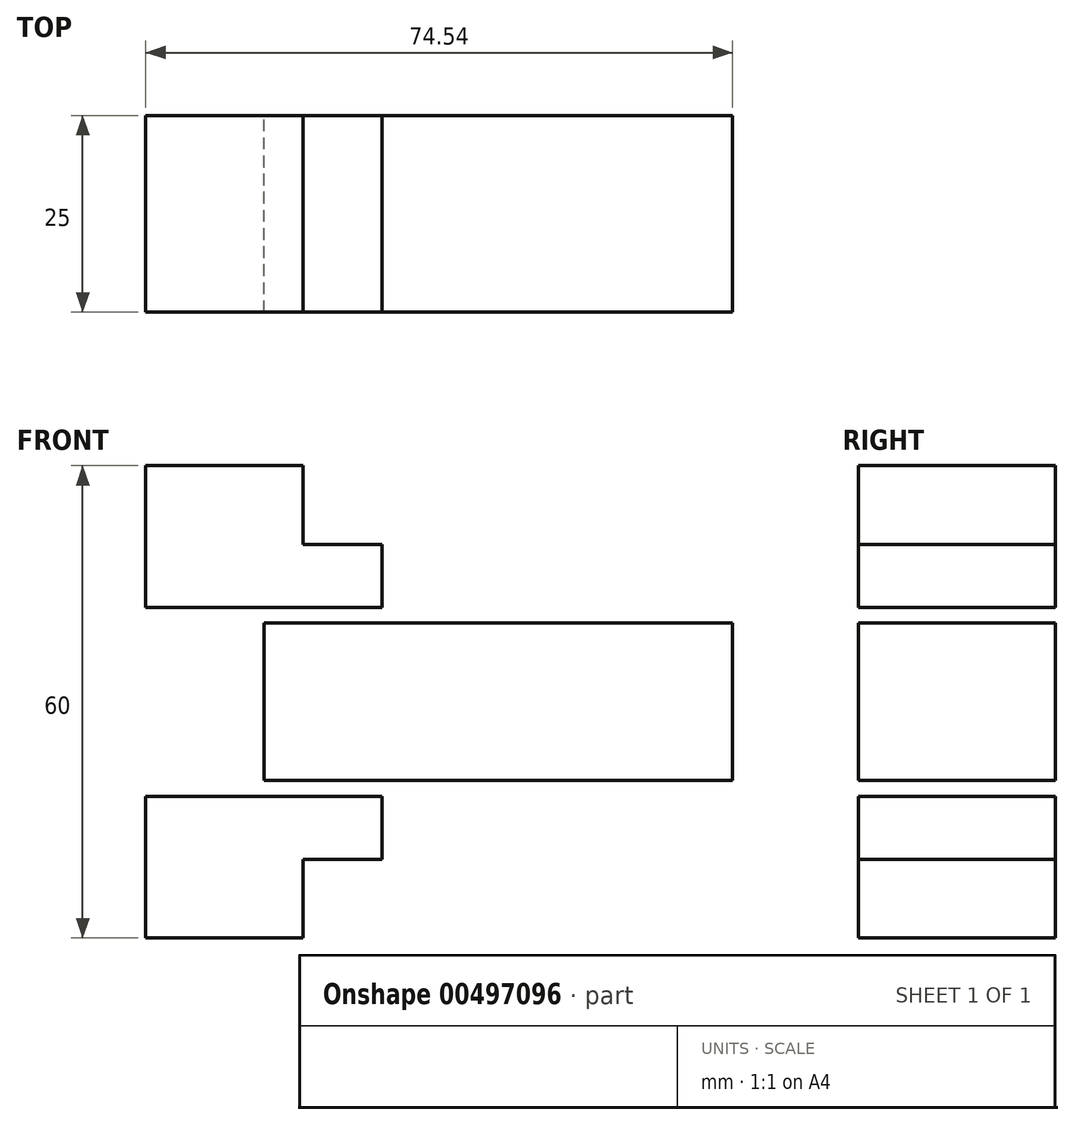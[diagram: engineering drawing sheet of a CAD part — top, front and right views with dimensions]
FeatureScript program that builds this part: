
annotation { "Feature Type Name" : "Feature", "Feature Type Description" : "" }
export const myFeature = defineFeature(function(context is Context, id is Id, definition is map)
    precondition{}
    {
        {
            var Q0;
            Q0=qCreatedBy(makeId("Front.planeOp"),FACE);
            var sketch = newSketch(context, id + "F0", { "sketchPlane" : qUnion([Q0])});
            skLineSegment(sketch, "E0.bottom", {"start": v(45, 30) * mm, "end": v(65, 30) * mm});
            skLineSegment(sketch, "E0.top", {"start": v(45, 20) * mm, "end": v(65, 20) * mm});
            skLineSegment(sketch, "E0.left", {"start": v(45, 30) * mm, "end": v(45, 20) * mm});
            skLineSegment(sketch, "E0.right", {"start": v(65, 30) * mm, "end": v(65, 20) * mm});
            skLineSegment(sketch, "E1.bottom", {"start": v(45, 20) * mm, "end": v(75, 20) * mm});
            skLineSegment(sketch, "E1.top", {"start": v(45, 12) * mm, "end": v(75, 12) * mm});
            skLineSegment(sketch, "E1.left", {"start": v(45, 20) * mm, "end": v(45, 12) * mm});
            skLineSegment(sketch, "E1.right", {"start": v(75, 20) * mm, "end": v(75, 12) * mm});
            skLineSegment(sketch, "E2.bottom", {"start": v(119.54, 10) * mm, "end": v(60, 10) * mm});
            skLineSegment(sketch, "E2.top", {"start": v(119.54, -10) * mm, "end": v(60, -10) * mm});
            skLineSegment(sketch, "E2.left", {"start": v(119.54, 10) * mm, "end": v(119.54, -10) * mm});
            skLineSegment(sketch, "E2.right", {"start": v(60, 10) * mm, "end": v(60, -10) * mm});
            skPoint(sketch, "E2.middle", {"position": v(89.77, 0) * mm});
            skLineSegment(sketch, "E3", {"start": v(159.4, 0) * mm, "end": v(184.94, 0) * mm, "construction": true});
            skPoint(sketch, "E3.startSnap0", {"position": v(119.54, 0) * mm});
            skPoint(sketch, "E3.endSnap0", {"position": v(119.54, 0) * mm});
            skLineSegment(sketch, "E4.MirrorCS", {"start": v(45, -20) * mm, "end": v(65, -20) * mm});
            skLineSegment(sketch, "E5.MirrorCS", {"start": v(45, -30) * mm, "end": v(65, -30) * mm});
            skLineSegment(sketch, "E6.MirrorCS", {"start": v(65, -30) * mm, "end": v(65, -20) * mm});
            skLineSegment(sketch, "E7.MirrorCS", {"start": v(45, -30) * mm, "end": v(45, -20) * mm});
            skLineSegment(sketch, "E8.MirrorCS", {"start": v(45, -20) * mm, "end": v(75, -20) * mm});
            skLineSegment(sketch, "E9.MirrorCS", {"start": v(45, -12) * mm, "end": v(75, -12) * mm});
            skLineSegment(sketch, "E10.MirrorCS", {"start": v(75, -20) * mm, "end": v(75, -12) * mm});
            skLineSegment(sketch, "E11.MirrorCS", {"start": v(45, -20) * mm, "end": v(45, -12) * mm});
            skSolve(sketch);
        }
        {
            var Q0;
            Q0 = qSketchRegion(id + "F0", true);
            extrude(context, id + "F1", {"entities" : qUnion([Q0]), "depth" : 25 * mm, "offsetDistance" : 25 * mm});
        }
    });
